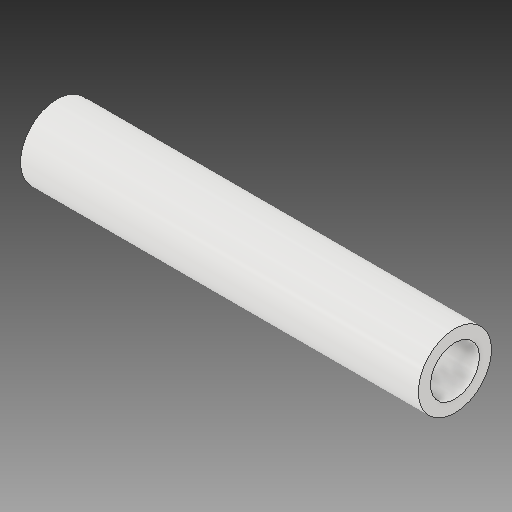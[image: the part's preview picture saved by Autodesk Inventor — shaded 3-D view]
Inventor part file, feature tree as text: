
AUTODESK INVENTOR PART (.ipt)
format: ipt  version: 2017.3 (Build 213256000, 256)  size: 95,744 bytes
history: native  units: mm
features: extrude x1, sketch x1
ambient origin geometry x8: Origin, YZ Plane, XZ Plane, XY Plane, X Axis, Y Axis, Z Axis, Center Point
bodies: Body1 (feature_tree)
feature tree (2):
  extrude  "Extrusion3"  Depth=13.0mm
  sketch  "Sketch4"  dims[d12=2.39mm d13=1.6mm d14=13.0mm d15=0.0mm]
